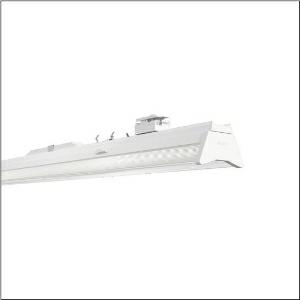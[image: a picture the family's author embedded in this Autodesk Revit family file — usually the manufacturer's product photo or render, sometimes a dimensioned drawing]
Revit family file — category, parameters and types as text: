
# Revit family: licross_r__11_performance_mo_51tm16mn4axg_6102
name_source: partatom
category: Lighting Fixtures
units: mm (PartAtom-declared; Revit-internal decimal feet)

## family parameters
Cut with Voids When Loaded = No
Host = Face
Light Source = No
Part Type = Normal
Room Calculation Point = No
Round Connector Dimension = Use Diameter
Shared = No

## types (1)
- --- (1 x LED, 10160 lm, 55.3 W, 4000K)
    Apparent Load = 55 VA
    CIE Flux Codes = 66 88 96 79 100
    Color Rendering = 80
    Color Temperature = 4000K
    Default Elevation = 1800 mm
    Description = Licross® 11 Performance MO, luminaire insert, of sheet steel, galvanised, coil coated, white, length: 1.500mm, width: 120mm, height: 123mm, LED rated luminous flux: 10.160lm, light colour: 840, control gear: ON/OFF Multilumen, with plug, 3-pole, with phase selection, mains connection: 220..240V, AC, 50/60Hz, rated input power: 55W, internal wiring halogen-free, primary light control with lens, of plastic, primary optical cover: cover, of PMMA, light emission: direct/indirect distribution, primary light characteristic: symmetric, protection rating (complete): IP40, insulation class (complete): insulation class I (protective earthing), certification: CE, ENEC, VDE, UKCA, protection symbol: D if used in an environment without relevant dust loads with corresponding accessories, impact resistance: IK06, permissible ambient temperature for indoor applications: -35..+40°C, corresponds to IFS (International Featured Standards) requirements for safety and quality in the food industry, reducing of maximum allowable ambient temperature of 5°C with ceiling mounting, LABS conformity tested according to VDMA 24364:2018-05, packaging unit: 1 piece
    Height = 114 mm
    Lamp = 1 x LED
    Lamp Light Flux = 10160 lm
    Lamp Power = 55.3 W
    Lamp count = 1
    Length = 1500 mm
    Luminous efficacy = 184 lm/W
    Manufacturer = Siteco
    ModVariant = No
    Model = 51TM16MN4AXG
    Mounting Place = Ceiling
    Mounting Type = Pendant
    Number of Poles = 1
    OnlyDefault = Yes
    Power Factor = 1
    Product Name = Licross® 11 Performance MO
    Product group = luminaire insert | ceiling pendant
    ProductGroupID = 902
    Protection Class = Protection class I
    Protection Degree = IP 40
    RLX_Detail_Level = 1
    RLX_Emergency_Light_Flux = 0 lm
    RLX_Emergency_Type = 0
    RLX_Emergency_Type_DB = No
    RlxData = <blob elided: 31853 chars, md5=bb1cd4e6>
    Socket = socket
    Standby Power = 0 W
    System Light Flux = 10160 lm
    System Power = 55 W
    Type Comments = factory setting: luminous flux: 100 % | (A | C | E) | 126 mA
    Type Image = l_1256138.jpg
    URL = http://relux.com
    VarID = @adj_107639
    Voltage = 0 V
    Weight = 0.00 kg
    Width = 120 mm

## geometry (parser evidence)
native form markers: Blend x4, Sweep x13
no freeform markers — native parametric forms only
